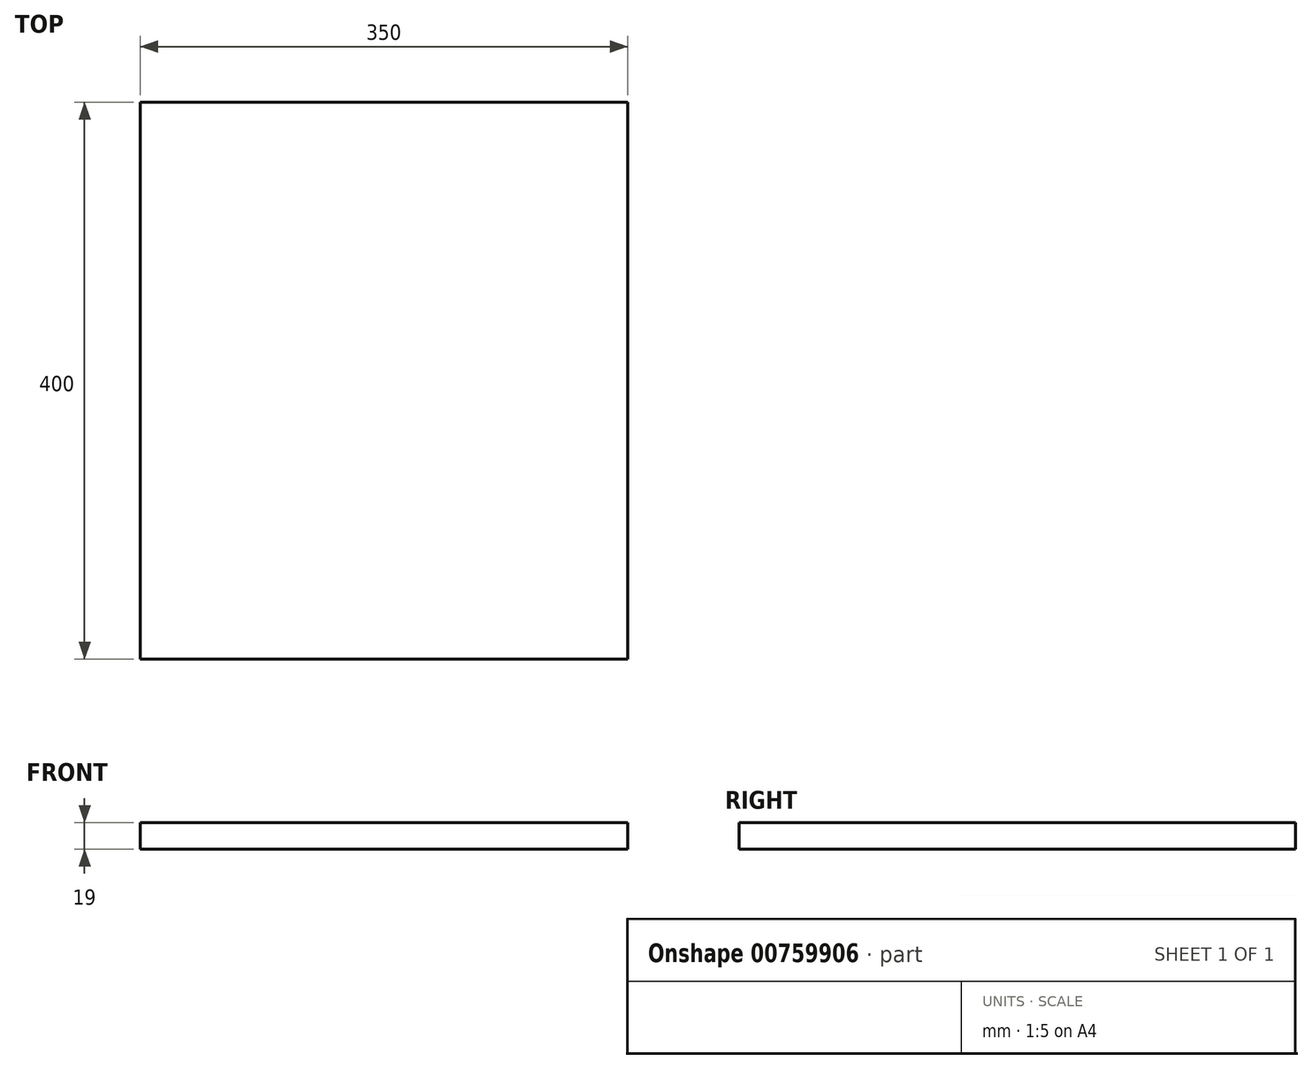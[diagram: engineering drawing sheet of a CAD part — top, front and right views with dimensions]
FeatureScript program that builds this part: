
annotation { "Feature Type Name" : "Feature", "Feature Type Description" : "" }
export const myFeature = defineFeature(function(context is Context, id is Id, definition is map)
    precondition{}
    {
        {
            var Q0;
            Q0=qCreatedBy(makeId("Top.planeOp"),FACE);
            var sketch = newSketch(context, id + "F0", { "sketchPlane" : qUnion([Q0])});
            skLineSegment(sketch, "E0.bottom", {"start": v(175, 200) * mm, "end": v(-175, 200) * mm});
            skLineSegment(sketch, "E0.top", {"start": v(175, -200) * mm, "end": v(-175, -200) * mm});
            skLineSegment(sketch, "E0.left", {"start": v(175, 200) * mm, "end": v(175, -200) * mm});
            skLineSegment(sketch, "E0.right", {"start": v(-175, 200) * mm, "end": v(-175, -200) * mm});
            skPoint(sketch, "E0.middle", {"position": v(0, 0) * mm});
            skSolve(sketch);
        }
        {
            var Q0;
            Q0=makeQuery(id+"F0.imprint","IMPRINT",FACE,{"disambiguationData":[TD([[makeQuery(id+"F0.imprint","IMPRINT",EDGE,{"derivedFrom":sQuery(id+"F0.wireOp",EDGE,"E0.bottom")}),1.0]])]});
            extrude(context, id + "F1", {"entities" : qUnion([Q0]), "depth" : 19 * mm, "offsetDistance" : 25 * mm});
        }
    });
